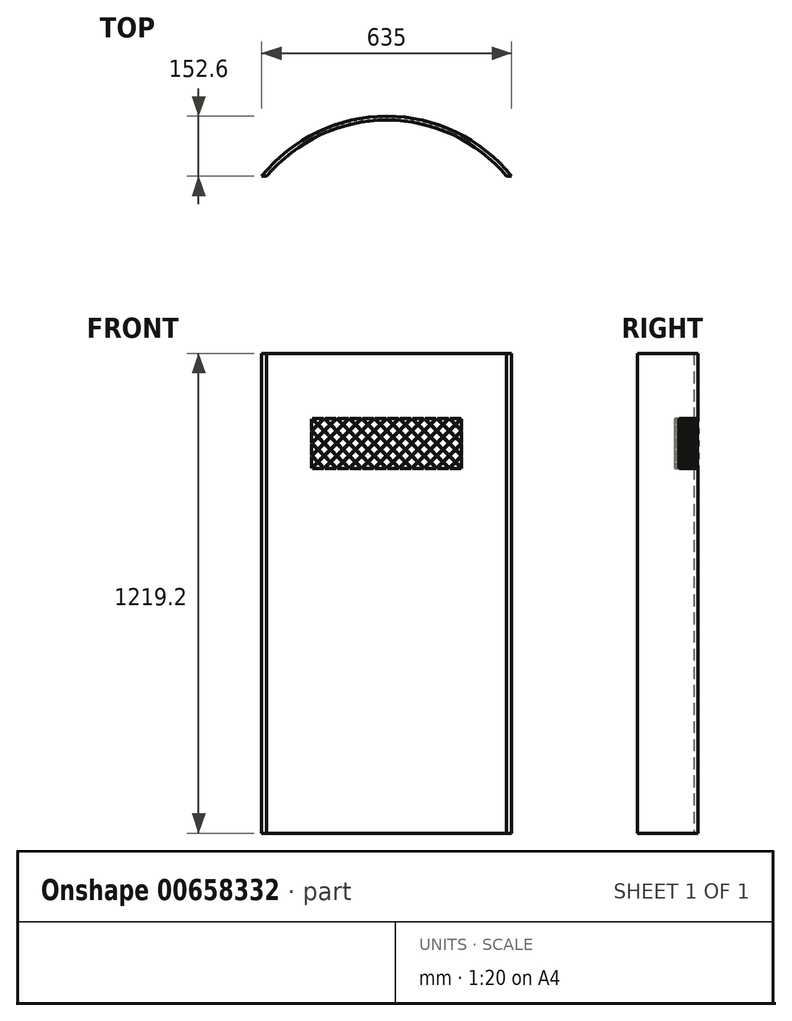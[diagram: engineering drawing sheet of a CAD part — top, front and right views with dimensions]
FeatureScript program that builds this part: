
annotation { "Feature Type Name" : "Feature", "Feature Type Description" : "" }
export const myFeature = defineFeature(function(context is Context, id is Id, definition is map)
    precondition{}
    {
        {
            var Q0;
            Q0=qCreatedBy(makeId("Top.planeOp"),FACE);
            var sketch = newSketch(context, id + "F0", { "sketchPlane" : qUnion([Q0])});
            skArc(sketch, "E0", {"start": v(304.8, 0) * mm, "mid": v(0, 142.76) * mm, "end": v(-304.8, 0) * mm});
            skArc(sketch, "E1", {"start": v(317.5, 0) * mm, "mid": v(0, 152.6) * mm, "end": v(-317.5, 0) * mm});
            skLineSegment(sketch, "E2", {"start": v(317.5, 0) * mm, "end": v(304.8, 0) * mm});
            skLineSegment(sketch, "E3", {"start": v(-304.8, 0) * mm, "end": v(-317.5, 0) * mm});
            skSolve(sketch);
        }
        {
            var Q0;
            Q0 = qSketchRegion(id + "F0", true);
            extrude(context, id + "F1", {"entities" : qUnion([Q0]), "depth" : 1219.2 * mm, "offsetDistance" : 25.4 * mm});
        }
        {
            var Q0;
            Q0=qCreatedBy(makeId("Front.planeOp"),FACE);
            var sketch = newSketch(context, id + "F2", { "sketchPlane" : qUnion([Q0])});
            skLineSegment(sketch, "E4.bottom", {"start": v(190.5, 1054.1) * mm, "end": v(-190.5, 1054.1) * mm});
            skLineSegment(sketch, "E4.top", {"start": v(190.5, 927.1) * mm, "end": v(-190.5, 927.1) * mm});
            skLineSegment(sketch, "E4.left", {"start": v(190.5, 1054.1) * mm, "end": v(190.5, 927.1) * mm});
            skLineSegment(sketch, "E4.right", {"start": v(-190.5, 1054.1) * mm, "end": v(-190.5, 927.1) * mm});
            skPoint(sketch, "E4.middle", {"position": v(0, 990.6) * mm});
            skPoint(sketch, "E5.orphan", {"position": v(-190.5, 990.6) * mm});
            skPoint(sketch, "E6.orphan", {"position": v(-63.5, 1054.1) * mm});
            skPoint(sketch, "E7.orphan", {"position": v(0, 927.1) * mm});
            skPoint(sketch, "E8.orphan", {"position": v(63.5, 1054.1) * mm});
            skPoint(sketch, "E9.end.orphan", {"position": v(190.5, 990.6) * mm});
            skPoint(sketch, "E10", {"position": v(63.5, 927.1) * mm});
            skPoint(sketch, "E11", {"position": v(-63.5, 927.1) * mm});
            skPoint(sketch, "E12", {"position": v(0, 1054.1) * mm});
            skPoint(sketch, "E13", {"position": v(127, 927.1) * mm});
            skPoint(sketch, "E14", {"position": v(127, 1054.1) * mm});
            skPoint(sketch, "E15", {"position": v(-127, 927.1) * mm});
            skPoint(sketch, "E16", {"position": v(-127, 1054.1) * mm});
            skPoint(sketch, "E17", {"position": v(190.5, 1022.35) * mm});
            skPoint(sketch, "E18", {"position": v(190.5, 958.85) * mm});
            skPoint(sketch, "E19", {"position": v(158.75, 927.1) * mm});
            skPoint(sketch, "E20", {"position": v(158.75, 1054.1) * mm});
            skPoint(sketch, "E21", {"position": v(95.25, 1054.1) * mm});
            skPoint(sketch, "E22", {"position": v(95.25, 927.1) * mm});
            skPoint(sketch, "E23", {"position": v(31.75, 927.1) * mm});
            skPoint(sketch, "E24", {"position": v(31.75, 1054.1) * mm});
            skPoint(sketch, "E25", {"position": v(-31.75, 1054.1) * mm});
            skPoint(sketch, "E26", {"position": v(-31.75, 927.1) * mm});
            skPoint(sketch, "E27", {"position": v(-95.25, 1054.1) * mm});
            skPoint(sketch, "E28", {"position": v(-95.25, 927.1) * mm});
            skPoint(sketch, "E29", {"position": v(-158.75, 927.1) * mm});
            skPoint(sketch, "E30", {"position": v(-158.75, 1054.1) * mm});
            skPoint(sketch, "E31", {"position": v(-190.5, 1022.35) * mm});
            skPoint(sketch, "E32", {"position": v(-190.5, 958.85) * mm});
            skLineSegment(sketch, "E33", {"start": v(-190.5, 1022.35) * mm, "end": v(-158.75, 1054.1) * mm});
            skLineSegment(sketch, "E34", {"start": v(-127, 1054.1) * mm, "end": v(-190.5, 990.6) * mm});
            skLineSegment(sketch, "E35", {"start": v(-190.5, 958.85) * mm, "end": v(-95.25, 1054.1) * mm});
            skLineSegment(sketch, "E36", {"start": v(-63.5, 1054.1) * mm, "end": v(-190.5, 927.1) * mm});
            skLineSegment(sketch, "E37", {"start": v(-158.75, 927.1) * mm, "end": v(-31.75, 1054.1) * mm});
            skLineSegment(sketch, "E38", {"start": v(0, 1054.1) * mm, "end": v(-127, 927.1) * mm});
            skLineSegment(sketch, "E39", {"start": v(-95.25, 927.1) * mm, "end": v(31.75, 1054.1) * mm});
            skLineSegment(sketch, "E40", {"start": v(63.5, 1054.1) * mm, "end": v(-63.5, 927.1) * mm});
            skLineSegment(sketch, "E41", {"start": v(-31.75, 927.1) * mm, "end": v(95.25, 1054.1) * mm});
            skLineSegment(sketch, "E42", {"start": v(127, 1054.1) * mm, "end": v(0, 927.1) * mm});
            skLineSegment(sketch, "E43", {"start": v(31.75, 927.1) * mm, "end": v(158.75, 1054.1) * mm});
            skLineSegment(sketch, "E44", {"start": v(190.5, 1054.1) * mm, "end": v(63.5, 927.1) * mm});
            skLineSegment(sketch, "E45", {"start": v(95.25, 927.1) * mm, "end": v(190.5, 1022.35) * mm});
            skLineSegment(sketch, "E46", {"start": v(190.5, 990.6) * mm, "end": v(127, 927.1) * mm});
            skLineSegment(sketch, "E47", {"start": v(127, 927.1) * mm, "end": v(158.75, 927.1) * mm});
            skLineSegment(sketch, "E48", {"start": v(158.75, 927.1) * mm, "end": v(158.75, 927.1) * mm});
            skLineSegment(sketch, "E49", {"start": v(190.5, 958.85) * mm, "end": v(158.75, 927.1) * mm});
            skLineSegment(sketch, "E50", {"start": v(190.5, 1022.35) * mm, "end": v(158.75, 1054.1) * mm});
            skLineSegment(sketch, "E51", {"start": v(127, 1054.1) * mm, "end": v(190.5, 990.6) * mm});
            skLineSegment(sketch, "E52", {"start": v(190.5, 958.85) * mm, "end": v(95.25, 1054.1) * mm});
            skLineSegment(sketch, "E53", {"start": v(190.5, 927.1) * mm, "end": v(63.5, 1054.1) * mm});
            skLineSegment(sketch, "E54", {"start": v(158.75, 927.1) * mm, "end": v(31.75, 1054.1) * mm});
            skLineSegment(sketch, "E55", {"start": v(0, 1054.1) * mm, "end": v(127, 927.1) * mm});
            skLineSegment(sketch, "E56", {"start": v(95.25, 927.1) * mm, "end": v(-31.75, 1054.1) * mm});
            skLineSegment(sketch, "E57", {"start": v(-63.5, 1054.1) * mm, "end": v(63.5, 927.1) * mm});
            skLineSegment(sketch, "E58", {"start": v(-95.25, 1054.1) * mm, "end": v(31.75, 927.1) * mm});
            skLineSegment(sketch, "E59", {"start": v(0, 927.1) * mm, "end": v(-127, 1054.1) * mm});
            skLineSegment(sketch, "E60", {"start": v(-158.75, 1054.1) * mm, "end": v(-31.75, 927.1) * mm});
            skLineSegment(sketch, "E61", {"start": v(-63.5, 927.1) * mm, "end": v(-190.5, 1054.1) * mm});
            skLineSegment(sketch, "E62", {"start": v(-190.5, 1022.35) * mm, "end": v(-95.25, 927.1) * mm});
            skLineSegment(sketch, "E63", {"start": v(-127, 927.1) * mm, "end": v(-190.5, 990.6) * mm});
            skLineSegment(sketch, "E64", {"start": v(-190.5, 958.85) * mm, "end": v(-158.75, 927.1) * mm});
            skLineSegment(sketch, "E65", {"start": v(-190.5, 1023.94) * mm, "end": v(-160.34, 1054.1) * mm});
            skLineSegment(sketch, "E66", {"start": v(-160.34, 1054.1) * mm, "end": v(-33.34, 927.1) * mm});
            skLineSegment(sketch, "E67", {"start": v(-33.34, 927.1) * mm, "end": v(93.66, 1054.1) * mm});
            skLineSegment(sketch, "E68", {"start": v(93.66, 1054.1) * mm, "end": v(190.5, 957.26) * mm});
            skLineSegment(sketch, "E69", {"start": v(190.5, 957.26) * mm, "end": v(160.34, 927.1) * mm});
            skLineSegment(sketch, "E70", {"start": v(160.34, 927.1) * mm, "end": v(33.34, 1054.1) * mm});
            skLineSegment(sketch, "E71", {"start": v(33.34, 1054.1) * mm, "end": v(-93.66, 927.1) * mm});
            skLineSegment(sketch, "E72", {"start": v(-93.66, 927.1) * mm, "end": v(-190.5, 1023.94) * mm});
            skLineSegment(sketch, "E73", {"start": v(-190.5, 1020.76) * mm, "end": v(-157.16, 1054.1) * mm});
            skLineSegment(sketch, "E74", {"start": v(-157.16, 1054.1) * mm, "end": v(-30.16, 927.1) * mm});
            skLineSegment(sketch, "E75", {"start": v(-30.16, 927.1) * mm, "end": v(96.84, 1054.1) * mm});
            skLineSegment(sketch, "E76", {"start": v(96.84, 1054.1) * mm, "end": v(190.5, 960.44) * mm});
            skLineSegment(sketch, "E77", {"start": v(190.5, 960.44) * mm, "end": v(157.16, 927.1) * mm});
            skLineSegment(sketch, "E78", {"start": v(157.16, 927.1) * mm, "end": v(30.16, 1054.1) * mm});
            skLineSegment(sketch, "E79", {"start": v(30.16, 1054.1) * mm, "end": v(-96.84, 927.1) * mm});
            skLineSegment(sketch, "E80", {"start": v(-96.84, 927.1) * mm, "end": v(-190.5, 1020.76) * mm});
            skLineSegment(sketch, "E81", {"start": v(-190.5, 992.19) * mm, "end": v(-128.59, 1054.1) * mm});
            skLineSegment(sketch, "E82", {"start": v(-128.59, 1054.1) * mm, "end": v(-1.59, 927.1) * mm});
            skLineSegment(sketch, "E83", {"start": v(-1.59, 927.1) * mm, "end": v(125.41, 1054.1) * mm});
            skLineSegment(sketch, "E84", {"start": v(125.41, 1054.1) * mm, "end": v(190.5, 989.01) * mm});
            skLineSegment(sketch, "E85", {"start": v(190.5, 989.01) * mm, "end": v(128.59, 927.1) * mm});
            skLineSegment(sketch, "E86", {"start": v(128.59, 927.1) * mm, "end": v(1.59, 1054.1) * mm});
            skLineSegment(sketch, "E87", {"start": v(1.59, 1054.1) * mm, "end": v(-125.41, 927.1) * mm});
            skLineSegment(sketch, "E88", {"start": v(-125.41, 927.1) * mm, "end": v(-190.5, 992.19) * mm});
            skLineSegment(sketch, "E89", {"start": v(-190.5, 989.01) * mm, "end": v(-125.41, 1054.1) * mm});
            skLineSegment(sketch, "E90", {"start": v(-125.41, 1054.1) * mm, "end": v(1.59, 927.1) * mm});
            skLineSegment(sketch, "E91", {"start": v(1.59, 927.1) * mm, "end": v(128.59, 1054.1) * mm});
            skLineSegment(sketch, "E92", {"start": v(128.59, 1054.1) * mm, "end": v(190.5, 992.19) * mm});
            skLineSegment(sketch, "E93", {"start": v(190.5, 992.19) * mm, "end": v(125.41, 927.1) * mm});
            skLineSegment(sketch, "E94", {"start": v(125.41, 927.1) * mm, "end": v(-1.59, 1054.1) * mm});
            skLineSegment(sketch, "E95", {"start": v(-1.59, 1054.1) * mm, "end": v(-128.59, 927.1) * mm});
            skLineSegment(sketch, "E96", {"start": v(-128.59, 927.1) * mm, "end": v(-190.5, 989.01) * mm});
            skLineSegment(sketch, "E97", {"start": v(-190.5, 960.44) * mm, "end": v(-96.84, 1054.1) * mm});
            skLineSegment(sketch, "E98", {"start": v(-96.84, 1054.1) * mm, "end": v(30.16, 927.1) * mm});
            skLineSegment(sketch, "E99", {"start": v(30.16, 927.1) * mm, "end": v(157.16, 1054.1) * mm});
            skLineSegment(sketch, "E100", {"start": v(157.16, 1054.1) * mm, "end": v(190.5, 1020.76) * mm});
            skLineSegment(sketch, "E101", {"start": v(190.5, 1020.76) * mm, "end": v(96.84, 927.1) * mm});
            skLineSegment(sketch, "E102", {"start": v(96.84, 927.1) * mm, "end": v(-30.16, 1054.1) * mm});
            skLineSegment(sketch, "E103", {"start": v(-30.16, 1054.1) * mm, "end": v(-157.16, 927.1) * mm});
            skLineSegment(sketch, "E104", {"start": v(-157.16, 927.1) * mm, "end": v(-190.5, 960.44) * mm});
            skLineSegment(sketch, "E105", {"start": v(-190.5, 957.26) * mm, "end": v(-93.66, 1054.1) * mm});
            skLineSegment(sketch, "E106", {"start": v(-93.66, 1054.1) * mm, "end": v(33.34, 927.1) * mm});
            skLineSegment(sketch, "E107", {"start": v(33.34, 927.1) * mm, "end": v(160.34, 1054.1) * mm});
            skLineSegment(sketch, "E108", {"start": v(160.34, 1054.1) * mm, "end": v(190.5, 1023.94) * mm});
            skLineSegment(sketch, "E109", {"start": v(190.5, 1023.94) * mm, "end": v(93.66, 927.1) * mm});
            skLineSegment(sketch, "E110", {"start": v(93.66, 927.1) * mm, "end": v(-33.34, 1054.1) * mm});
            skLineSegment(sketch, "E111", {"start": v(-33.34, 1054.1) * mm, "end": v(-160.34, 927.1) * mm});
            skLineSegment(sketch, "E112", {"start": v(-160.34, 927.1) * mm, "end": v(-190.5, 957.26) * mm});
            skLineSegment(sketch, "E113", {"start": v(-190.5, 928.69) * mm, "end": v(-65.09, 1054.1) * mm});
            skLineSegment(sketch, "E114", {"start": v(-65.09, 1054.1) * mm, "end": v(61.91, 927.1) * mm});
            skLineSegment(sketch, "E115", {"start": v(61.91, 927.1) * mm, "end": v(188.91, 1054.1) * mm});
            skLineSegment(sketch, "E116", {"start": v(190.5, 1052.51) * mm, "end": v(65.09, 927.1) * mm});
            skLineSegment(sketch, "E117", {"start": v(65.09, 927.1) * mm, "end": v(-61.91, 1054.1) * mm});
            skLineSegment(sketch, "E118", {"start": v(-61.91, 1054.1) * mm, "end": v(-188.91, 927.1) * mm});
            skLineSegment(sketch, "E119", {"start": v(-188.91, 1054.1) * mm, "end": v(-61.91, 927.1) * mm});
            skLineSegment(sketch, "E120", {"start": v(-61.91, 927.1) * mm, "end": v(65.09, 1054.1) * mm});
            skLineSegment(sketch, "E121", {"start": v(65.09, 1054.1) * mm, "end": v(190.5, 928.69) * mm});
            skLineSegment(sketch, "E122", {"start": v(188.91, 927.1) * mm, "end": v(61.91, 1054.1) * mm});
            skLineSegment(sketch, "E123", {"start": v(61.91, 1054.1) * mm, "end": v(-65.09, 927.1) * mm});
            skLineSegment(sketch, "E124", {"start": v(-65.09, 927.1) * mm, "end": v(-190.5, 1052.51) * mm});
            skSolve(sketch);
        }
        {
            var Q0;
            {var subQ0=sQuery(id+"F2.wireOp",EDGE,"E117");var subQ1=sQuery(id+"F2.wireOp",EDGE,"E75");var subQ2=makeQuery(id+"F2.imprint","INTERSECT",VERTEX,{"derivedFrom":[subQ1,subQ0]});Q0=makeQuery(id+"F2.imprint","IMPRINT",FACE,{"disambiguationData":[TD([[makeQuery(id+"F2.imprint","IMPRINT",EDGE,{"disambiguationData":[TD([[subQ2,-1.0]])],"derivedFrom":subQ1}),-1.0]])]});}
            var Q1;
            {var subQ0=sQuery(id+"F2.wireOp",EDGE,"E91");var subQ1=sQuery(id+"F2.wireOp",EDGE,"E76");var subQ2=makeQuery(id+"F2.imprint","INTERSECT",VERTEX,{"derivedFrom":[subQ1,subQ0]});Q1=makeQuery(id+"F2.imprint","IMPRINT",FACE,{"disambiguationData":[TD([[makeQuery(id+"F2.imprint","IMPRINT",EDGE,{"disambiguationData":[TD([[subQ2,-1.0]])],"derivedFrom":subQ1}),1.0]])]});}
            var Q2;
            {var subQ0=sQuery(id+"F2.wireOp",EDGE,"E86");var subQ1=sQuery(id+"F2.wireOp",EDGE,"E75");var subQ2=makeQuery(id+"F2.imprint","INTERSECT",VERTEX,{"derivedFrom":[subQ1,subQ0]});Q2=makeQuery(id+"F2.imprint","IMPRINT",FACE,{"disambiguationData":[TD([[makeQuery(id+"F2.imprint","IMPRINT",EDGE,{"disambiguationData":[TD([[subQ2,-1.0]])],"derivedFrom":subQ1}),-1.0]])]});}
            var Q3;
            {var subQ1=sQuery(id+"F2.wireOp",EDGE,"E4.top");var subQ3=sQuery(id+"F2.wireOp",EDGE,"E122");var subQ4=makeQuery(id+"F2.imprint","INTERSECT",VERTEX,{"derivedFrom":[subQ1,subQ3]});Q3=makeQuery(id+"F2.imprint","IMPRINT",FACE,{"disambiguationData":[TD([[makeQuery(id+"F2.imprint","IMPRINT",EDGE,{"disambiguationData":[TD([[subQ4,-1.0]])],"derivedFrom":subQ3}),1.0]])]});}
            var Q4;
            {var subQ0=sQuery(id+"F2.wireOp",EDGE,"E102");var subQ1=sQuery(id+"F2.wireOp",EDGE,"E67");var subQ2=makeQuery(id+"F2.imprint","INTERSECT",VERTEX,{"derivedFrom":[subQ1,subQ0]});Q4=makeQuery(id+"F2.imprint","IMPRINT",FACE,{"disambiguationData":[TD([[makeQuery(id+"F2.imprint","IMPRINT",EDGE,{"disambiguationData":[TD([[subQ2,-1.0]])],"derivedFrom":subQ1}),1.0]])]});}
            var Q5;
            {var subQ0=sQuery(id+"F2.wireOp",EDGE,"E80");var subQ3=sQuery(id+"F2.wireOp",EDGE,"E87");var subQ5=makeQuery(id+"F2.imprint","INTERSECT",VERTEX,{"derivedFrom":[subQ0,subQ3]});Q5=makeQuery(id+"F2.imprint","IMPRINT",FACE,{"disambiguationData":[TD([[makeQuery(id+"F2.imprint","IMPRINT",EDGE,{"disambiguationData":[TD([[subQ5,1.0]])],"derivedFrom":subQ0}),1.0]])]});}
            var Q6;
            {var subQ0=sQuery(id+"F2.wireOp",EDGE,"E92");var subQ3=sQuery(id+"F2.wireOp",EDGE,"E99");var subQ5=makeQuery(id+"F2.imprint","INTERSECT",VERTEX,{"derivedFrom":[subQ0,subQ3]});Q6=makeQuery(id+"F2.imprint","IMPRINT",FACE,{"disambiguationData":[TD([[makeQuery(id+"F2.imprint","IMPRINT",EDGE,{"disambiguationData":[TD([[subQ5,1.0]])],"derivedFrom":subQ0}),1.0]])]});}
            var Q7;
            {var subQ0=sQuery(id+"F2.wireOp",EDGE,"E103");var subQ1=sQuery(id+"F2.wireOp",EDGE,"E90");var subQ2=makeQuery(id+"F2.imprint","INTERSECT",VERTEX,{"derivedFrom":[subQ1,subQ0]});Q7=makeQuery(id+"F2.imprint","IMPRINT",FACE,{"disambiguationData":[TD([[makeQuery(id+"F2.imprint","IMPRINT",EDGE,{"disambiguationData":[TD([[subQ2,-1.0]])],"derivedFrom":subQ1}),1.0]])]});}
            var Q8;
            {var subQ0=sQuery(id+"F2.wireOp",EDGE,"E106");var subQ1=sQuery(id+"F2.wireOp",EDGE,"E75");var subQ2=makeQuery(id+"F2.imprint","INTERSECT",VERTEX,{"derivedFrom":[subQ1,subQ0]});Q8=makeQuery(id+"F2.imprint","IMPRINT",FACE,{"disambiguationData":[TD([[makeQuery(id+"F2.imprint","IMPRINT",EDGE,{"disambiguationData":[TD([[subQ2,-1.0]])],"derivedFrom":subQ1}),-1.0]])]});}
            var Q9;
            {var subQ0=sQuery(id+"F2.wireOp",EDGE,"E114");var subQ1=sQuery(id+"F2.wireOp",EDGE,"E79");var subQ2=makeQuery(id+"F2.imprint","INTERSECT",VERTEX,{"derivedFrom":[subQ1,subQ0]});Q9=makeQuery(id+"F2.imprint","IMPRINT",FACE,{"disambiguationData":[TD([[makeQuery(id+"F2.imprint","IMPRINT",EDGE,{"disambiguationData":[TD([[subQ2,-1.0]])],"derivedFrom":subQ1}),-1.0]])]});}
            var Q10;
            {var subQ0=sQuery(id+"F2.wireOp",EDGE,"E87");var subQ1=sQuery(id+"F2.wireOp",EDGE,"E66");var subQ2=makeQuery(id+"F2.imprint","INTERSECT",VERTEX,{"derivedFrom":[subQ1,subQ0]});Q10=makeQuery(id+"F2.imprint","IMPRINT",FACE,{"disambiguationData":[TD([[makeQuery(id+"F2.imprint","IMPRINT",EDGE,{"disambiguationData":[TD([[subQ2,-1.0]])],"derivedFrom":subQ1}),-1.0]])]});}
            var Q11;
            {var subQ0=sQuery(id+"F2.wireOp",EDGE,"E74");var subQ1=sQuery(id+"F2.wireOp",EDGE,"E67");var subQ2=makeQuery(id+"F2.imprint","INTERSECT",VERTEX,{"derivedFrom":[subQ1,subQ0]});Q11=makeQuery(id+"F2.imprint","IMPRINT",FACE,{"disambiguationData":[TD([[makeQuery(id+"F2.imprint","IMPRINT",EDGE,{"disambiguationData":[TD([[subQ2,-1.0]])],"derivedFrom":subQ1}),1.0]])]});}
            var Q12;
            {var subQ0=sQuery(id+"F2.wireOp",EDGE,"E75");var subQ3=sQuery(id+"F2.wireOp",EDGE,"E82");var subQ5=makeQuery(id+"F2.imprint","INTERSECT",VERTEX,{"derivedFrom":[subQ0,subQ3]});Q12=makeQuery(id+"F2.imprint","IMPRINT",FACE,{"disambiguationData":[TD([[makeQuery(id+"F2.imprint","IMPRINT",EDGE,{"disambiguationData":[TD([[subQ5,1.0]])],"derivedFrom":subQ0}),-1.0]])]});}
            var Q13;
            {var subQ0=sQuery(id+"F2.wireOp",EDGE,"E113");var subQ1=sQuery(id+"F2.wireOp",EDGE,"E96");var subQ2=makeQuery(id+"F2.imprint","INTERSECT",VERTEX,{"derivedFrom":[subQ1,subQ0]});Q13=makeQuery(id+"F2.imprint","IMPRINT",FACE,{"disambiguationData":[TD([[makeQuery(id+"F2.imprint","IMPRINT",EDGE,{"disambiguationData":[TD([[subQ2,-1.0]])],"derivedFrom":subQ1}),1.0]])]});}
            var Q14;
            {var subQ0=sQuery(id+"F2.wireOp",EDGE,"E90");var subQ3=sQuery(id+"F2.wireOp",EDGE,"E97");var subQ5=makeQuery(id+"F2.imprint","INTERSECT",VERTEX,{"derivedFrom":[subQ0,subQ3]});Q14=makeQuery(id+"F2.imprint","IMPRINT",FACE,{"disambiguationData":[TD([[makeQuery(id+"F2.imprint","IMPRINT",EDGE,{"disambiguationData":[TD([[subQ5,1.0]])],"derivedFrom":subQ0}),1.0]])]});}
            var Q15;
            {var subQ0=sQuery(id+"F2.wireOp",EDGE,"E102");var subQ1=sQuery(id+"F2.wireOp",EDGE,"E91");var subQ2=makeQuery(id+"F2.imprint","INTERSECT",VERTEX,{"derivedFrom":[subQ1,subQ0]});Q15=makeQuery(id+"F2.imprint","IMPRINT",FACE,{"disambiguationData":[TD([[makeQuery(id+"F2.imprint","IMPRINT",EDGE,{"disambiguationData":[TD([[subQ2,-1.0]])],"derivedFrom":subQ1}),-1.0]])]});}
            var Q16;
            {var subQ0=sQuery(id+"F2.wireOp",EDGE,"E78");var subQ3=sQuery(id+"F2.wireOp",EDGE,"E85");var subQ5=makeQuery(id+"F2.imprint","INTERSECT",VERTEX,{"derivedFrom":[subQ0,subQ3]});Q16=makeQuery(id+"F2.imprint","IMPRINT",FACE,{"disambiguationData":[TD([[makeQuery(id+"F2.imprint","IMPRINT",EDGE,{"disambiguationData":[TD([[subQ5,1.0]])],"derivedFrom":subQ0}),1.0]])]});}
            var Q17;
            {var subQ0=sQuery(id+"F2.wireOp",EDGE,"E109");var subQ1=sQuery(id+"F2.wireOp",EDGE,"E94");var subQ2=makeQuery(id+"F2.imprint","INTERSECT",VERTEX,{"derivedFrom":[subQ1,subQ0]});Q17=makeQuery(id+"F2.imprint","IMPRINT",FACE,{"disambiguationData":[TD([[makeQuery(id+"F2.imprint","IMPRINT",EDGE,{"disambiguationData":[TD([[subQ2,-1.0]])],"derivedFrom":subQ1}),1.0]])]});}
            var Q18;
            {var subQ0=sQuery(id+"F2.wireOp",EDGE,"E111");var subQ1=sQuery(id+"F2.wireOp",EDGE,"E80");var subQ2=makeQuery(id+"F2.imprint","INTERSECT",VERTEX,{"derivedFrom":[subQ1,subQ0]});Q18=makeQuery(id+"F2.imprint","IMPRINT",FACE,{"disambiguationData":[TD([[makeQuery(id+"F2.imprint","IMPRINT",EDGE,{"disambiguationData":[TD([[subQ2,-1.0]])],"derivedFrom":subQ1}),1.0]])]});}
            var Q19;
            {var subQ0=sQuery(id+"F2.wireOp",EDGE,"E96");var subQ3=sQuery(id+"F2.wireOp",EDGE,"E103");var subQ5=makeQuery(id+"F2.imprint","INTERSECT",VERTEX,{"derivedFrom":[subQ0,subQ3]});Q19=makeQuery(id+"F2.imprint","IMPRINT",FACE,{"disambiguationData":[TD([[makeQuery(id+"F2.imprint","IMPRINT",EDGE,{"disambiguationData":[TD([[subQ5,1.0]])],"derivedFrom":subQ0}),1.0]])]});}
            var Q20;
            {var subQ0=sQuery(id+"F2.wireOp",EDGE,"E111");var subQ3=sQuery(id+"F2.wireOp",EDGE,"E117");var subQ5=makeQuery(id+"F2.imprint","INTERSECT",VERTEX,{"derivedFrom":[subQ0,subQ3]});Q20=makeQuery(id+"F2.imprint","IMPRINT",FACE,{"disambiguationData":[TD([[makeQuery(id+"F2.imprint","IMPRINT",EDGE,{"disambiguationData":[TD([[subQ5,1.0]])],"derivedFrom":subQ0}),-1.0]])]});}
            var Q21;
            {var subQ0=sQuery(id+"F2.wireOp",EDGE,"E107");var subQ1=sQuery(id+"F2.wireOp",EDGE,"E92");var subQ2=makeQuery(id+"F2.imprint","INTERSECT",VERTEX,{"derivedFrom":[subQ1,subQ0]});Q21=makeQuery(id+"F2.imprint","IMPRINT",FACE,{"disambiguationData":[TD([[makeQuery(id+"F2.imprint","IMPRINT",EDGE,{"disambiguationData":[TD([[subQ2,-1.0]])],"derivedFrom":subQ1}),1.0]])]});}
            var Q22;
            {var subQ0=sQuery(id+"F2.wireOp",EDGE,"E78");var subQ1=sQuery(id+"F2.wireOp",EDGE,"E71");var subQ2=makeQuery(id+"F2.imprint","INTERSECT",VERTEX,{"derivedFrom":[subQ1,subQ0]});Q22=makeQuery(id+"F2.imprint","IMPRINT",FACE,{"disambiguationData":[TD([[makeQuery(id+"F2.imprint","IMPRINT",EDGE,{"disambiguationData":[TD([[subQ2,-1.0]])],"derivedFrom":subQ1}),1.0]])]});}
            var Q23;
            {var subQ0=sQuery(id+"F2.wireOp",EDGE,"E115");var subQ1=sQuery(id+"F2.wireOp",EDGE,"E78");var subQ2=makeQuery(id+"F2.imprint","INTERSECT",VERTEX,{"derivedFrom":[subQ1,subQ0]});Q23=makeQuery(id+"F2.imprint","IMPRINT",FACE,{"disambiguationData":[TD([[makeQuery(id+"F2.imprint","IMPRINT",EDGE,{"disambiguationData":[TD([[subQ2,-1.0]])],"derivedFrom":subQ1}),1.0]])]});}
            var Q24;
            {var subQ0=sQuery(id+"F2.wireOp",EDGE,"E109");var subQ1=sQuery(id+"F2.wireOp",EDGE,"E70");var subQ2=makeQuery(id+"F2.imprint","INTERSECT",VERTEX,{"derivedFrom":[subQ1,subQ0]});Q24=makeQuery(id+"F2.imprint","IMPRINT",FACE,{"disambiguationData":[TD([[makeQuery(id+"F2.imprint","IMPRINT",EDGE,{"disambiguationData":[TD([[subQ2,-1.0]])],"derivedFrom":subQ1}),-1.0]])]});}
            var Q25;
            {var subQ0=sQuery(id+"F2.wireOp",EDGE,"E96");var subQ3=sQuery(id+"F2.wireOp",EDGE,"E97");var subQ5=makeQuery(id+"F2.imprint","INTERSECT",VERTEX,{"derivedFrom":[subQ0,subQ3]});Q25=makeQuery(id+"F2.imprint","IMPRINT",FACE,{"disambiguationData":[TD([[makeQuery(id+"F2.imprint","IMPRINT",EDGE,{"disambiguationData":[TD([[subQ5,-1.0]])],"derivedFrom":subQ0}),1.0]])]});}
            var Q26;
            {var subQ1=sQuery(id+"F2.wireOp",EDGE,"E4.bottom");var subQ3=sQuery(id+"F2.wireOp",EDGE,"E115");var subQ4=makeQuery(id+"F2.imprint","INTERSECT",VERTEX,{"derivedFrom":[subQ1,subQ3]});Q26=makeQuery(id+"F2.imprint","IMPRINT",FACE,{"disambiguationData":[TD([[makeQuery(id+"F2.imprint","IMPRINT",EDGE,{"disambiguationData":[TD([[subQ4,1.0]])],"derivedFrom":subQ3}),1.0]])]});}
            var Q27;
            {var subQ0=sQuery(id+"F2.wireOp",EDGE,"E107");var subQ1=sQuery(id+"F2.wireOp",EDGE,"E68");var subQ2=makeQuery(id+"F2.imprint","INTERSECT",VERTEX,{"derivedFrom":[subQ1,subQ0]});Q27=makeQuery(id+"F2.imprint","IMPRINT",FACE,{"disambiguationData":[TD([[makeQuery(id+"F2.imprint","IMPRINT",EDGE,{"disambiguationData":[TD([[subQ2,-1.0]])],"derivedFrom":subQ1}),-1.0]])]});}
            var Q28;
            {var subQ0=sQuery(id+"F2.wireOp",EDGE,"E97");var subQ1=sQuery(id+"F2.wireOp",EDGE,"E80");var subQ2=makeQuery(id+"F2.imprint","INTERSECT",VERTEX,{"derivedFrom":[subQ1,subQ0]});Q28=makeQuery(id+"F2.imprint","IMPRINT",FACE,{"disambiguationData":[TD([[makeQuery(id+"F2.imprint","IMPRINT",EDGE,{"disambiguationData":[TD([[subQ2,-1.0]])],"derivedFrom":subQ1}),1.0]])]});}
            var Q29;
            {var subQ0=sQuery(id+"F2.wireOp",EDGE,"E71");var subQ3=sQuery(id+"F2.wireOp",EDGE,"E124");var subQ5=makeQuery(id+"F2.imprint","INTERSECT",VERTEX,{"derivedFrom":[subQ0,subQ3]});Q29=makeQuery(id+"F2.imprint","IMPRINT",FACE,{"disambiguationData":[TD([[makeQuery(id+"F2.imprint","IMPRINT",EDGE,{"disambiguationData":[TD([[subQ5,-1.0]])],"derivedFrom":subQ0}),1.0]])]});}
            var Q30;
            {var subQ0=sQuery(id+"F2.wireOp",EDGE,"E114");var subQ1=sQuery(id+"F2.wireOp",EDGE,"E71");var subQ2=makeQuery(id+"F2.imprint","INTERSECT",VERTEX,{"derivedFrom":[subQ1,subQ0]});Q30=makeQuery(id+"F2.imprint","IMPRINT",FACE,{"disambiguationData":[TD([[makeQuery(id+"F2.imprint","IMPRINT",EDGE,{"disambiguationData":[TD([[subQ2,-1.0]])],"derivedFrom":subQ1}),1.0]])]});}
            var Q31;
            {var subQ0=sQuery(id+"F2.wireOp",EDGE,"E102");var subQ1=sQuery(id+"F2.wireOp",EDGE,"E75");var subQ2=makeQuery(id+"F2.imprint","INTERSECT",VERTEX,{"derivedFrom":[subQ1,subQ0]});Q31=makeQuery(id+"F2.imprint","IMPRINT",FACE,{"disambiguationData":[TD([[makeQuery(id+"F2.imprint","IMPRINT",EDGE,{"disambiguationData":[TD([[subQ2,-1.0]])],"derivedFrom":subQ1}),-1.0]])]});}
            var Q32;
            {var subQ0=sQuery(id+"F2.wireOp",EDGE,"E117");var subQ1=sQuery(id+"F2.wireOp",EDGE,"E107");var subQ2=makeQuery(id+"F2.imprint","INTERSECT",VERTEX,{"derivedFrom":[subQ1,subQ0]});Q32=makeQuery(id+"F2.imprint","IMPRINT",FACE,{"disambiguationData":[TD([[makeQuery(id+"F2.imprint","IMPRINT",EDGE,{"disambiguationData":[TD([[subQ2,-1.0]])],"derivedFrom":subQ1}),-1.0]])]});}
            var Q33;
            {var subQ0=sQuery(id+"F2.wireOp",EDGE,"E77");var subQ1=sQuery(id+"F2.wireOp",EDGE,"E70");var subQ2=makeQuery(id+"F2.imprint","INTERSECT",VERTEX,{"derivedFrom":[subQ1,subQ0]});Q33=makeQuery(id+"F2.imprint","IMPRINT",FACE,{"disambiguationData":[TD([[makeQuery(id+"F2.imprint","IMPRINT",EDGE,{"disambiguationData":[TD([[subQ2,-1.0]])],"derivedFrom":subQ1}),-1.0]])]});}
            var Q34;
            {var subQ0=sQuery(id+"F2.wireOp",EDGE,"E97");var subQ1=sQuery(id+"F2.wireOp",EDGE,"E72");var subQ2=makeQuery(id+"F2.imprint","INTERSECT",VERTEX,{"derivedFrom":[subQ1,subQ0]});Q34=makeQuery(id+"F2.imprint","IMPRINT",FACE,{"disambiguationData":[TD([[makeQuery(id+"F2.imprint","IMPRINT",EDGE,{"disambiguationData":[TD([[subQ2,-1.0]])],"derivedFrom":subQ1}),-1.0]])]});}
            var Q35;
            {var subQ0=sQuery(id+"F2.wireOp",EDGE,"E118");var subQ1=sQuery(id+"F2.wireOp",EDGE,"E90");var subQ2=makeQuery(id+"F2.imprint","INTERSECT",VERTEX,{"derivedFrom":[subQ1,subQ0]});Q35=makeQuery(id+"F2.imprint","IMPRINT",FACE,{"disambiguationData":[TD([[makeQuery(id+"F2.imprint","IMPRINT",EDGE,{"disambiguationData":[TD([[subQ2,-1.0]])],"derivedFrom":subQ1}),1.0]])]});}
            var Q36;
            {var subQ0=sQuery(id+"F2.wireOp",EDGE,"E107");var subQ1=sQuery(id+"F2.wireOp",EDGE,"E76");var subQ2=makeQuery(id+"F2.imprint","INTERSECT",VERTEX,{"derivedFrom":[subQ1,subQ0]});Q36=makeQuery(id+"F2.imprint","IMPRINT",FACE,{"disambiguationData":[TD([[makeQuery(id+"F2.imprint","IMPRINT",EDGE,{"disambiguationData":[TD([[subQ2,-1.0]])],"derivedFrom":subQ1}),1.0]])]});}
            var Q37;
            {var subQ1=sQuery(id+"F2.wireOp",EDGE,"E4.right");var subQ3=sQuery(id+"F2.wireOp",EDGE,"E113");var subQ4=makeQuery(id+"F2.imprint","INTERSECT",VERTEX,{"derivedFrom":[subQ1,subQ3]});Q37=makeQuery(id+"F2.imprint","IMPRINT",FACE,{"disambiguationData":[TD([[makeQuery(id+"F2.imprint","IMPRINT",EDGE,{"disambiguationData":[TD([[subQ4,-1.0]])],"derivedFrom":subQ3}),1.0]])]});}
            var Q38;
            {var subQ0=sQuery(id+"F2.wireOp",EDGE,"E76");var subQ3=sQuery(id+"F2.wireOp",EDGE,"E85");var subQ5=makeQuery(id+"F2.imprint","INTERSECT",VERTEX,{"derivedFrom":[subQ0,subQ3]});Q38=makeQuery(id+"F2.imprint","IMPRINT",FACE,{"disambiguationData":[TD([[makeQuery(id+"F2.imprint","IMPRINT",EDGE,{"disambiguationData":[TD([[subQ5,-1.0]])],"derivedFrom":subQ0}),1.0]])]});}
            var Q39;
            {var subQ0=sQuery(id+"F2.wireOp",EDGE,"E110");var subQ1=sQuery(id+"F2.wireOp",EDGE,"E71");var subQ2=makeQuery(id+"F2.imprint","INTERSECT",VERTEX,{"derivedFrom":[subQ1,subQ0]});Q39=makeQuery(id+"F2.imprint","IMPRINT",FACE,{"disambiguationData":[TD([[makeQuery(id+"F2.imprint","IMPRINT",EDGE,{"disambiguationData":[TD([[subQ2,-1.0]])],"derivedFrom":subQ1}),1.0]])]});}
            var Q40;
            {var subQ0=sQuery(id+"F2.wireOp",EDGE,"E82");var subQ1=sQuery(id+"F2.wireOp",EDGE,"E71");var subQ2=makeQuery(id+"F2.imprint","INTERSECT",VERTEX,{"derivedFrom":[subQ1,subQ0]});Q40=makeQuery(id+"F2.imprint","IMPRINT",FACE,{"disambiguationData":[TD([[makeQuery(id+"F2.imprint","IMPRINT",EDGE,{"disambiguationData":[TD([[subQ2,-1.0]])],"derivedFrom":subQ1}),1.0]])]});}
            var Q41;
            {var subQ0=sQuery(id+"F2.wireOp",EDGE,"E111");var subQ1=sQuery(id+"F2.wireOp",EDGE,"E96");var subQ2=makeQuery(id+"F2.imprint","INTERSECT",VERTEX,{"derivedFrom":[subQ1,subQ0]});Q41=makeQuery(id+"F2.imprint","IMPRINT",FACE,{"disambiguationData":[TD([[makeQuery(id+"F2.imprint","IMPRINT",EDGE,{"disambiguationData":[TD([[subQ2,-1.0]])],"derivedFrom":subQ1}),1.0]])]});}
            var Q42;
            {var subQ0=sQuery(id+"F2.wireOp",EDGE,"E109");var subQ1=sQuery(id+"F2.wireOp",EDGE,"E78");var subQ2=makeQuery(id+"F2.imprint","INTERSECT",VERTEX,{"derivedFrom":[subQ1,subQ0]});Q42=makeQuery(id+"F2.imprint","IMPRINT",FACE,{"disambiguationData":[TD([[makeQuery(id+"F2.imprint","IMPRINT",EDGE,{"disambiguationData":[TD([[subQ2,-1.0]])],"derivedFrom":subQ1}),1.0]])]});}
            var Q43;
            {var subQ0=sQuery(id+"F2.wireOp",EDGE,"E116");var subQ1=sQuery(id+"F2.wireOp",EDGE,"E76");var subQ2=makeQuery(id+"F2.imprint","INTERSECT",VERTEX,{"derivedFrom":[subQ1,subQ0]});Q43=makeQuery(id+"F2.imprint","IMPRINT",FACE,{"disambiguationData":[TD([[makeQuery(id+"F2.imprint","IMPRINT",EDGE,{"disambiguationData":[TD([[subQ2,-1.0]])],"derivedFrom":subQ1}),1.0]])]});}
            var Q44;
            {var subQ0=sQuery(id+"F2.wireOp",EDGE,"E99");var subQ1=sQuery(id+"F2.wireOp",EDGE,"E78");var subQ2=makeQuery(id+"F2.imprint","INTERSECT",VERTEX,{"derivedFrom":[subQ1,subQ0]});Q44=makeQuery(id+"F2.imprint","IMPRINT",FACE,{"disambiguationData":[TD([[makeQuery(id+"F2.imprint","IMPRINT",EDGE,{"disambiguationData":[TD([[subQ2,-1.0]])],"derivedFrom":subQ1}),1.0]])]});}
            var Q45;
            {var subQ0=sQuery(id+"F2.wireOp",EDGE,"E116");var subQ1=sQuery(id+"F2.wireOp",EDGE,"E92");var subQ2=makeQuery(id+"F2.imprint","INTERSECT",VERTEX,{"derivedFrom":[subQ1,subQ0]});Q45=makeQuery(id+"F2.imprint","IMPRINT",FACE,{"disambiguationData":[TD([[makeQuery(id+"F2.imprint","IMPRINT",EDGE,{"disambiguationData":[TD([[subQ2,-1.0]])],"derivedFrom":subQ1}),1.0]])]});}
            var Q46;
            {var subQ0=sQuery(id+"F2.wireOp",EDGE,"E101");var subQ1=sQuery(id+"F2.wireOp",EDGE,"E76");var subQ2=makeQuery(id+"F2.imprint","INTERSECT",VERTEX,{"derivedFrom":[subQ1,subQ0]});Q46=makeQuery(id+"F2.imprint","IMPRINT",FACE,{"disambiguationData":[TD([[makeQuery(id+"F2.imprint","IMPRINT",EDGE,{"disambiguationData":[TD([[subQ2,-1.0]])],"derivedFrom":subQ1}),1.0]])]});}
            var Q47;
            {var subQ0=sQuery(id+"F2.wireOp",EDGE,"E86");var subQ1=sQuery(id+"F2.wireOp",EDGE,"E67");var subQ2=makeQuery(id+"F2.imprint","INTERSECT",VERTEX,{"derivedFrom":[subQ1,subQ0]});Q47=makeQuery(id+"F2.imprint","IMPRINT",FACE,{"disambiguationData":[TD([[makeQuery(id+"F2.imprint","IMPRINT",EDGE,{"disambiguationData":[TD([[subQ2,-1.0]])],"derivedFrom":subQ1}),1.0]])]});}
            var Q48;
            {var subQ0=sQuery(id+"F2.wireOp",EDGE,"E94");var subQ1=sQuery(id+"F2.wireOp",EDGE,"E71");var subQ2=makeQuery(id+"F2.imprint","INTERSECT",VERTEX,{"derivedFrom":[subQ1,subQ0]});Q48=makeQuery(id+"F2.imprint","IMPRINT",FACE,{"disambiguationData":[TD([[makeQuery(id+"F2.imprint","IMPRINT",EDGE,{"disambiguationData":[TD([[subQ2,-1.0]])],"derivedFrom":subQ1}),1.0]])]});}
            var Q49;
            {var subQ0=sQuery(id+"F2.wireOp",EDGE,"E114");var subQ1=sQuery(id+"F2.wireOp",EDGE,"E95");var subQ2=makeQuery(id+"F2.imprint","INTERSECT",VERTEX,{"derivedFrom":[subQ1,subQ0]});Q49=makeQuery(id+"F2.imprint","IMPRINT",FACE,{"disambiguationData":[TD([[makeQuery(id+"F2.imprint","IMPRINT",EDGE,{"disambiguationData":[TD([[subQ2,-1.0]])],"derivedFrom":subQ1}),-1.0]])]});}
            var Q50;
            {var subQ0=sQuery(id+"F2.wireOp",EDGE,"E67");var subQ3=sQuery(id+"F2.wireOp",EDGE,"E121");var subQ5=makeQuery(id+"F2.imprint","INTERSECT",VERTEX,{"derivedFrom":[subQ0,subQ3]});Q50=makeQuery(id+"F2.imprint","IMPRINT",FACE,{"disambiguationData":[TD([[makeQuery(id+"F2.imprint","IMPRINT",EDGE,{"disambiguationData":[TD([[subQ5,-1.0]])],"derivedFrom":subQ0}),1.0]])]});}
            var Q51;
            {var subQ0=sQuery(id+"F2.wireOp",EDGE,"E118");var subQ1=sQuery(id+"F2.wireOp",EDGE,"E74");var subQ2=makeQuery(id+"F2.imprint","INTERSECT",VERTEX,{"derivedFrom":[subQ1,subQ0]});Q51=makeQuery(id+"F2.imprint","IMPRINT",FACE,{"disambiguationData":[TD([[makeQuery(id+"F2.imprint","IMPRINT",EDGE,{"disambiguationData":[TD([[subQ2,-1.0]])],"derivedFrom":subQ1}),1.0]])]});}
            var Q52;
            {var subQ0=sQuery(id+"F2.wireOp",EDGE,"E93");var subQ1=sQuery(id+"F2.wireOp",EDGE,"E78");var subQ2=makeQuery(id+"F2.imprint","INTERSECT",VERTEX,{"derivedFrom":[subQ1,subQ0]});Q52=makeQuery(id+"F2.imprint","IMPRINT",FACE,{"disambiguationData":[TD([[makeQuery(id+"F2.imprint","IMPRINT",EDGE,{"disambiguationData":[TD([[subQ2,-1.0]])],"derivedFrom":subQ1}),1.0]])]});}
            var Q53;
            {var subQ0=sQuery(id+"F2.wireOp",EDGE,"E110");var subQ1=sQuery(id+"F2.wireOp",EDGE,"E95");var subQ2=makeQuery(id+"F2.imprint","INTERSECT",VERTEX,{"derivedFrom":[subQ1,subQ0]});Q53=makeQuery(id+"F2.imprint","IMPRINT",FACE,{"disambiguationData":[TD([[makeQuery(id+"F2.imprint","IMPRINT",EDGE,{"disambiguationData":[TD([[subQ2,-1.0]])],"derivedFrom":subQ1}),-1.0]])]});}
            var Q54;
            {var subQ0=sQuery(id+"F2.wireOp",EDGE,"E99");var subQ1=sQuery(id+"F2.wireOp",EDGE,"E70");var subQ2=makeQuery(id+"F2.imprint","INTERSECT",VERTEX,{"derivedFrom":[subQ1,subQ0]});Q54=makeQuery(id+"F2.imprint","IMPRINT",FACE,{"disambiguationData":[TD([[makeQuery(id+"F2.imprint","IMPRINT",EDGE,{"disambiguationData":[TD([[subQ2,-1.0]])],"derivedFrom":subQ1}),-1.0]])]});}
            var Q55;
            {var subQ0=sQuery(id+"F2.wireOp",EDGE,"E70");var subQ3=sQuery(id+"F2.wireOp",EDGE,"E123");var subQ5=makeQuery(id+"F2.imprint","INTERSECT",VERTEX,{"derivedFrom":[subQ0,subQ3]});Q55=makeQuery(id+"F2.imprint","IMPRINT",FACE,{"disambiguationData":[TD([[makeQuery(id+"F2.imprint","IMPRINT",EDGE,{"disambiguationData":[TD([[subQ5,-1.0]])],"derivedFrom":subQ0}),-1.0]])]});}
            var Q56;
            {var subQ0=sQuery(id+"F2.wireOp",EDGE,"E105");var subQ1=sQuery(id+"F2.wireOp",EDGE,"E90");var subQ2=makeQuery(id+"F2.imprint","INTERSECT",VERTEX,{"derivedFrom":[subQ1,subQ0]});Q56=makeQuery(id+"F2.imprint","IMPRINT",FACE,{"disambiguationData":[TD([[makeQuery(id+"F2.imprint","IMPRINT",EDGE,{"disambiguationData":[TD([[subQ2,-1.0]])],"derivedFrom":subQ1}),1.0]])]});}
            var Q57;
            {var subQ0=sQuery(id+"F2.wireOp",EDGE,"E113");var subQ1=sQuery(id+"F2.wireOp",EDGE,"E72");var subQ2=makeQuery(id+"F2.imprint","INTERSECT",VERTEX,{"derivedFrom":[subQ1,subQ0]});Q57=makeQuery(id+"F2.imprint","IMPRINT",FACE,{"disambiguationData":[TD([[makeQuery(id+"F2.imprint","IMPRINT",EDGE,{"disambiguationData":[TD([[subQ2,-1.0]])],"derivedFrom":subQ1}),-1.0]])]});}
            var Q58;
            {var subQ0=sQuery(id+"F2.wireOp",EDGE,"E94");var subQ1=sQuery(id+"F2.wireOp",EDGE,"E79");var subQ2=makeQuery(id+"F2.imprint","INTERSECT",VERTEX,{"derivedFrom":[subQ1,subQ0]});Q58=makeQuery(id+"F2.imprint","IMPRINT",FACE,{"disambiguationData":[TD([[makeQuery(id+"F2.imprint","IMPRINT",EDGE,{"disambiguationData":[TD([[subQ2,-1.0]])],"derivedFrom":subQ1}),-1.0]])]});}
            var Q59;
            {var subQ0=sQuery(id+"F2.wireOp",EDGE,"E103");var subQ1=sQuery(id+"F2.wireOp",EDGE,"E74");var subQ2=makeQuery(id+"F2.imprint","INTERSECT",VERTEX,{"derivedFrom":[subQ1,subQ0]});Q59=makeQuery(id+"F2.imprint","IMPRINT",FACE,{"disambiguationData":[TD([[makeQuery(id+"F2.imprint","IMPRINT",EDGE,{"disambiguationData":[TD([[subQ2,-1.0]])],"derivedFrom":subQ1}),1.0]])]});}
            var Q60;
            {var subQ0=sQuery(id+"F2.wireOp",EDGE,"E83");var subQ1=sQuery(id+"F2.wireOp",EDGE,"E70");var subQ2=makeQuery(id+"F2.imprint","INTERSECT",VERTEX,{"derivedFrom":[subQ1,subQ0]});Q60=makeQuery(id+"F2.imprint","IMPRINT",FACE,{"disambiguationData":[TD([[makeQuery(id+"F2.imprint","IMPRINT",EDGE,{"disambiguationData":[TD([[subQ2,-1.0]])],"derivedFrom":subQ1}),-1.0]])]});}
            var Q61;
            {var subQ0=sQuery(id+"F2.wireOp",EDGE,"E107");var subQ3=sQuery(id+"F2.wireOp",EDGE,"E114");var subQ5=makeQuery(id+"F2.imprint","INTERSECT",VERTEX,{"derivedFrom":[subQ0,subQ3]});Q61=makeQuery(id+"F2.imprint","IMPRINT",FACE,{"disambiguationData":[TD([[makeQuery(id+"F2.imprint","IMPRINT",EDGE,{"disambiguationData":[TD([[subQ5,1.0]])],"derivedFrom":subQ0}),-1.0]])]});}
            var Q62;
            {var subQ0=sQuery(id+"F2.wireOp",EDGE,"E103");var subQ1=sQuery(id+"F2.wireOp",EDGE,"E66");var subQ2=makeQuery(id+"F2.imprint","INTERSECT",VERTEX,{"derivedFrom":[subQ1,subQ0]});Q62=makeQuery(id+"F2.imprint","IMPRINT",FACE,{"disambiguationData":[TD([[makeQuery(id+"F2.imprint","IMPRINT",EDGE,{"disambiguationData":[TD([[subQ2,-1.0]])],"derivedFrom":subQ1}),-1.0]])]});}
            var Q63;
            {var subQ1=sQuery(id+"F2.wireOp",EDGE,"E4.bottom");var subQ3=sQuery(id+"F2.wireOp",EDGE,"E119");var subQ4=makeQuery(id+"F2.imprint","INTERSECT",VERTEX,{"derivedFrom":[subQ1,subQ3]});Q63=makeQuery(id+"F2.imprint","IMPRINT",FACE,{"disambiguationData":[TD([[makeQuery(id+"F2.imprint","IMPRINT",EDGE,{"disambiguationData":[TD([[subQ4,-1.0]])],"derivedFrom":subQ3}),1.0]])]});}
            var Q64;
            {var subQ0=sQuery(id+"F2.wireOp",EDGE,"E76");var subQ3=sQuery(id+"F2.wireOp",EDGE,"E83");var subQ5=makeQuery(id+"F2.imprint","INTERSECT",VERTEX,{"derivedFrom":[subQ0,subQ3]});Q64=makeQuery(id+"F2.imprint","IMPRINT",FACE,{"disambiguationData":[TD([[makeQuery(id+"F2.imprint","IMPRINT",EDGE,{"disambiguationData":[TD([[subQ5,1.0]])],"derivedFrom":subQ0}),1.0]])]});}
            var Q65;
            {var subQ0=sQuery(id+"F2.wireOp",EDGE,"E71");var subQ1=sQuery(id+"F2.wireOp",EDGE,"E66");var subQ2=makeQuery(id+"F2.imprint","INTERSECT",VERTEX,{"derivedFrom":[subQ1,subQ0]});Q65=makeQuery(id+"F2.imprint","IMPRINT",FACE,{"disambiguationData":[TD([[makeQuery(id+"F2.imprint","IMPRINT",EDGE,{"disambiguationData":[TD([[subQ2,-1.0]])],"derivedFrom":subQ1}),-1.0]])]});}
            var Q66;
            {var subQ0=sQuery(id+"F2.wireOp",EDGE,"E118");var subQ1=sQuery(id+"F2.wireOp",EDGE,"E66");var subQ2=makeQuery(id+"F2.imprint","INTERSECT",VERTEX,{"derivedFrom":[subQ1,subQ0]});Q66=makeQuery(id+"F2.imprint","IMPRINT",FACE,{"disambiguationData":[TD([[makeQuery(id+"F2.imprint","IMPRINT",EDGE,{"disambiguationData":[TD([[subQ2,-1.0]])],"derivedFrom":subQ1}),-1.0]])]});}
            var Q67;
            {var subQ0=sQuery(id+"F2.wireOp",EDGE,"E95");var subQ1=sQuery(id+"F2.wireOp",EDGE,"E72");var subQ2=makeQuery(id+"F2.imprint","INTERSECT",VERTEX,{"derivedFrom":[subQ1,subQ0]});Q67=makeQuery(id+"F2.imprint","IMPRINT",FACE,{"disambiguationData":[TD([[makeQuery(id+"F2.imprint","IMPRINT",EDGE,{"disambiguationData":[TD([[subQ2,-1.0]])],"derivedFrom":subQ1}),-1.0]])]});}
            var Q68;
            {var subQ0=sQuery(id+"F2.wireOp",EDGE,"E85");var subQ1=sQuery(id+"F2.wireOp",EDGE,"E68");var subQ2=makeQuery(id+"F2.imprint","INTERSECT",VERTEX,{"derivedFrom":[subQ1,subQ0]});Q68=makeQuery(id+"F2.imprint","IMPRINT",FACE,{"disambiguationData":[TD([[makeQuery(id+"F2.imprint","IMPRINT",EDGE,{"disambiguationData":[TD([[subQ2,-1.0]])],"derivedFrom":subQ1}),-1.0]])]});}
            var Q69;
            {var subQ1=sQuery(id+"F2.wireOp",EDGE,"E4.top");var subQ3=sQuery(id+"F2.wireOp",EDGE,"E118");var subQ4=makeQuery(id+"F2.imprint","INTERSECT",VERTEX,{"derivedFrom":[subQ1,subQ3]});Q69=makeQuery(id+"F2.imprint","IMPRINT",FACE,{"disambiguationData":[TD([[makeQuery(id+"F2.imprint","IMPRINT",EDGE,{"disambiguationData":[TD([[subQ4,1.0]])],"derivedFrom":subQ3}),1.0]])]});}
            var Q70;
            {var subQ0=sQuery(id+"F2.wireOp",EDGE,"E115");var subQ1=sQuery(id+"F2.wireOp",EDGE,"E70");var subQ2=makeQuery(id+"F2.imprint","INTERSECT",VERTEX,{"derivedFrom":[subQ1,subQ0]});Q70=makeQuery(id+"F2.imprint","IMPRINT",FACE,{"disambiguationData":[TD([[makeQuery(id+"F2.imprint","IMPRINT",EDGE,{"disambiguationData":[TD([[subQ2,-1.0]])],"derivedFrom":subQ1}),-1.0]])]});}
            var Q71;
            {var subQ0=sQuery(id+"F2.wireOp",EDGE,"E89");var subQ1=sQuery(id+"F2.wireOp",EDGE,"E66");var subQ2=makeQuery(id+"F2.imprint","INTERSECT",VERTEX,{"derivedFrom":[subQ1,subQ0]});Q71=makeQuery(id+"F2.imprint","IMPRINT",FACE,{"disambiguationData":[TD([[makeQuery(id+"F2.imprint","IMPRINT",EDGE,{"disambiguationData":[TD([[subQ2,-1.0]])],"derivedFrom":subQ1}),-1.0]])]});}
            var Q72;
            {var subQ0=sQuery(id+"F2.wireOp",EDGE,"E105");var subQ1=sQuery(id+"F2.wireOp",EDGE,"E74");var subQ2=makeQuery(id+"F2.imprint","INTERSECT",VERTEX,{"derivedFrom":[subQ1,subQ0]});Q72=makeQuery(id+"F2.imprint","IMPRINT",FACE,{"disambiguationData":[TD([[makeQuery(id+"F2.imprint","IMPRINT",EDGE,{"disambiguationData":[TD([[subQ2,-1.0]])],"derivedFrom":subQ1}),1.0]])]});}
            var Q73;
            {var subQ0=sQuery(id+"F2.wireOp",EDGE,"E106");var subQ1=sQuery(id+"F2.wireOp",EDGE,"E91");var subQ2=makeQuery(id+"F2.imprint","INTERSECT",VERTEX,{"derivedFrom":[subQ1,subQ0]});Q73=makeQuery(id+"F2.imprint","IMPRINT",FACE,{"disambiguationData":[TD([[makeQuery(id+"F2.imprint","IMPRINT",EDGE,{"disambiguationData":[TD([[subQ2,-1.0]])],"derivedFrom":subQ1}),-1.0]])]});}
            var Q74;
            {var subQ1=sQuery(id+"F2.wireOp",EDGE,"E4.left");var subQ3=sQuery(id+"F2.wireOp",EDGE,"E116");var subQ4=makeQuery(id+"F2.imprint","INTERSECT",VERTEX,{"derivedFrom":[subQ1,subQ3]});Q74=makeQuery(id+"F2.imprint","IMPRINT",FACE,{"disambiguationData":[TD([[makeQuery(id+"F2.imprint","IMPRINT",EDGE,{"disambiguationData":[TD([[subQ4,-1.0]])],"derivedFrom":subQ3}),1.0]])]});}
            var Q75;
            {var subQ1=sQuery(id+"F2.wireOp",EDGE,"E4.right");var subQ3=sQuery(id+"F2.wireOp",EDGE,"E124");var subQ4=makeQuery(id+"F2.imprint","INTERSECT",VERTEX,{"derivedFrom":[subQ1,subQ3]});Q75=makeQuery(id+"F2.imprint","IMPRINT",FACE,{"disambiguationData":[TD([[makeQuery(id+"F2.imprint","IMPRINT",EDGE,{"disambiguationData":[TD([[subQ4,1.0]])],"derivedFrom":subQ3}),1.0]])]});}
            var Q76;
            {var subQ0=sQuery(id+"F2.wireOp",EDGE,"E80");var subQ3=sQuery(id+"F2.wireOp",EDGE,"E81");var subQ5=makeQuery(id+"F2.imprint","INTERSECT",VERTEX,{"derivedFrom":[subQ0,subQ3]});Q76=makeQuery(id+"F2.imprint","IMPRINT",FACE,{"disambiguationData":[TD([[makeQuery(id+"F2.imprint","IMPRINT",EDGE,{"disambiguationData":[TD([[subQ5,-1.0]])],"derivedFrom":subQ0}),1.0]])]});}
            var Q77;
            {var subQ0=sQuery(id+"F2.wireOp",EDGE,"E73");var subQ1=sQuery(id+"F2.wireOp",EDGE,"E66");var subQ2=makeQuery(id+"F2.imprint","INTERSECT",VERTEX,{"derivedFrom":[subQ1,subQ0]});Q77=makeQuery(id+"F2.imprint","IMPRINT",FACE,{"disambiguationData":[TD([[makeQuery(id+"F2.imprint","IMPRINT",EDGE,{"disambiguationData":[TD([[subQ2,-1.0]])],"derivedFrom":subQ1}),-1.0]])]});}
            var Q78;
            {var subQ0=sQuery(id+"F2.wireOp",EDGE,"E79");var subQ3=sQuery(id+"F2.wireOp",EDGE,"E86");var subQ5=makeQuery(id+"F2.imprint","INTERSECT",VERTEX,{"derivedFrom":[subQ0,subQ3]});Q78=makeQuery(id+"F2.imprint","IMPRINT",FACE,{"disambiguationData":[TD([[makeQuery(id+"F2.imprint","IMPRINT",EDGE,{"disambiguationData":[TD([[subQ5,1.0]])],"derivedFrom":subQ0}),-1.0]])]});}
            var Q79;
            {var subQ0=sQuery(id+"F2.wireOp",EDGE,"E110");var subQ1=sQuery(id+"F2.wireOp",EDGE,"E79");var subQ2=makeQuery(id+"F2.imprint","INTERSECT",VERTEX,{"derivedFrom":[subQ1,subQ0]});Q79=makeQuery(id+"F2.imprint","IMPRINT",FACE,{"disambiguationData":[TD([[makeQuery(id+"F2.imprint","IMPRINT",EDGE,{"disambiguationData":[TD([[subQ2,-1.0]])],"derivedFrom":subQ1}),-1.0]])]});}
            var Q80;
            {var subQ0=sQuery(id+"F2.wireOp",EDGE,"E95");var subQ1=sQuery(id+"F2.wireOp",EDGE,"E80");var subQ2=makeQuery(id+"F2.imprint","INTERSECT",VERTEX,{"derivedFrom":[subQ1,subQ0]});Q80=makeQuery(id+"F2.imprint","IMPRINT",FACE,{"disambiguationData":[TD([[makeQuery(id+"F2.imprint","IMPRINT",EDGE,{"disambiguationData":[TD([[subQ2,-1.0]])],"derivedFrom":subQ1}),1.0]])]});}
            var Q81;
            {var subQ0=sQuery(id+"F2.wireOp",EDGE,"E101");var subQ1=sQuery(id+"F2.wireOp",EDGE,"E68");var subQ2=makeQuery(id+"F2.imprint","INTERSECT",VERTEX,{"derivedFrom":[subQ1,subQ0]});Q81=makeQuery(id+"F2.imprint","IMPRINT",FACE,{"disambiguationData":[TD([[makeQuery(id+"F2.imprint","IMPRINT",EDGE,{"disambiguationData":[TD([[subQ2,-1.0]])],"derivedFrom":subQ1}),-1.0]])]});}
            var Q82;
            {var subQ0=sQuery(id+"F2.wireOp",EDGE,"E94");var subQ3=sQuery(id+"F2.wireOp",EDGE,"E101");var subQ5=makeQuery(id+"F2.imprint","INTERSECT",VERTEX,{"derivedFrom":[subQ0,subQ3]});Q82=makeQuery(id+"F2.imprint","IMPRINT",FACE,{"disambiguationData":[TD([[makeQuery(id+"F2.imprint","IMPRINT",EDGE,{"disambiguationData":[TD([[subQ5,1.0]])],"derivedFrom":subQ0}),1.0]])]});}
            var Q83;
            {var subQ0=sQuery(id+"F2.wireOp",EDGE,"E87");var subQ1=sQuery(id+"F2.wireOp",EDGE,"E74");var subQ2=makeQuery(id+"F2.imprint","INTERSECT",VERTEX,{"derivedFrom":[subQ1,subQ0]});Q83=makeQuery(id+"F2.imprint","IMPRINT",FACE,{"disambiguationData":[TD([[makeQuery(id+"F2.imprint","IMPRINT",EDGE,{"disambiguationData":[TD([[subQ2,-1.0]])],"derivedFrom":subQ1}),1.0]])]});}
            var Q84;
            {var subQ0=sQuery(id+"F2.wireOp",EDGE,"E91");var subQ3=sQuery(id+"F2.wireOp",EDGE,"E98");var subQ5=makeQuery(id+"F2.imprint","INTERSECT",VERTEX,{"derivedFrom":[subQ0,subQ3]});Q84=makeQuery(id+"F2.imprint","IMPRINT",FACE,{"disambiguationData":[TD([[makeQuery(id+"F2.imprint","IMPRINT",EDGE,{"disambiguationData":[TD([[subQ5,1.0]])],"derivedFrom":subQ0}),-1.0]])]});}
            var Q85;
            {var subQ0=sQuery(id+"F2.wireOp",EDGE,"E117");var subQ1=sQuery(id+"F2.wireOp",EDGE,"E67");var subQ2=makeQuery(id+"F2.imprint","INTERSECT",VERTEX,{"derivedFrom":[subQ1,subQ0]});Q85=makeQuery(id+"F2.imprint","IMPRINT",FACE,{"disambiguationData":[TD([[makeQuery(id+"F2.imprint","IMPRINT",EDGE,{"disambiguationData":[TD([[subQ2,-1.0]])],"derivedFrom":subQ1}),1.0]])]});}
            var Q86;
            {var subQ0=sQuery(id+"F2.wireOp",EDGE,"E81");var subQ1=sQuery(id+"F2.wireOp",EDGE,"E72");var subQ2=makeQuery(id+"F2.imprint","INTERSECT",VERTEX,{"derivedFrom":[subQ1,subQ0]});Q86=makeQuery(id+"F2.imprint","IMPRINT",FACE,{"disambiguationData":[TD([[makeQuery(id+"F2.imprint","IMPRINT",EDGE,{"disambiguationData":[TD([[subQ2,-1.0]])],"derivedFrom":subQ1}),-1.0]])]});}
            var Q87;
            {var subQ1=sQuery(id+"F2.wireOp",EDGE,"E4.left");var subQ3=sQuery(id+"F2.wireOp",EDGE,"E121");var subQ4=makeQuery(id+"F2.imprint","INTERSECT",VERTEX,{"derivedFrom":[subQ1,subQ3]});Q87=makeQuery(id+"F2.imprint","IMPRINT",FACE,{"disambiguationData":[TD([[makeQuery(id+"F2.imprint","IMPRINT",EDGE,{"disambiguationData":[TD([[subQ4,1.0]])],"derivedFrom":subQ3}),1.0]])]});}
            var Q88;
            {var subQ0=sQuery(id+"F2.wireOp",EDGE,"E74");var subQ3=sQuery(id+"F2.wireOp",EDGE,"E81");var subQ5=makeQuery(id+"F2.imprint","INTERSECT",VERTEX,{"derivedFrom":[subQ0,subQ3]});Q88=makeQuery(id+"F2.imprint","IMPRINT",FACE,{"disambiguationData":[TD([[makeQuery(id+"F2.imprint","IMPRINT",EDGE,{"disambiguationData":[TD([[subQ5,1.0]])],"derivedFrom":subQ0}),1.0]])]});}
            var Q89;
            {var subQ0=sQuery(id+"F2.wireOp",EDGE,"E95");var subQ3=sQuery(id+"F2.wireOp",EDGE,"E102");var subQ5=makeQuery(id+"F2.imprint","INTERSECT",VERTEX,{"derivedFrom":[subQ0,subQ3]});Q89=makeQuery(id+"F2.imprint","IMPRINT",FACE,{"disambiguationData":[TD([[makeQuery(id+"F2.imprint","IMPRINT",EDGE,{"disambiguationData":[TD([[subQ5,1.0]])],"derivedFrom":subQ0}),-1.0]])]});}
            var Q90;
            {var subQ0=sQuery(id+"F2.wireOp",EDGE,"E91");var subQ1=sQuery(id+"F2.wireOp",EDGE,"E68");var subQ2=makeQuery(id+"F2.imprint","INTERSECT",VERTEX,{"derivedFrom":[subQ1,subQ0]});Q90=makeQuery(id+"F2.imprint","IMPRINT",FACE,{"disambiguationData":[TD([[makeQuery(id+"F2.imprint","IMPRINT",EDGE,{"disambiguationData":[TD([[subQ2,-1.0]])],"derivedFrom":subQ1}),-1.0]])]});}
            var Q91;
            {var subQ0=sQuery(id+"F2.wireOp",EDGE,"E70");var subQ1=sQuery(id+"F2.wireOp",EDGE,"E67");var subQ2=makeQuery(id+"F2.imprint","INTERSECT",VERTEX,{"derivedFrom":[subQ1,subQ0]});Q91=makeQuery(id+"F2.imprint","IMPRINT",FACE,{"disambiguationData":[TD([[makeQuery(id+"F2.imprint","IMPRINT",EDGE,{"disambiguationData":[TD([[subQ2,-1.0]])],"derivedFrom":subQ1}),1.0]])]});}
            var Q92;
            {var subQ0=sQuery(id+"F2.wireOp",EDGE,"E118");var subQ1=sQuery(id+"F2.wireOp",EDGE,"E106");var subQ2=makeQuery(id+"F2.imprint","INTERSECT",VERTEX,{"derivedFrom":[subQ1,subQ0]});Q92=makeQuery(id+"F2.imprint","IMPRINT",FACE,{"disambiguationData":[TD([[makeQuery(id+"F2.imprint","IMPRINT",EDGE,{"disambiguationData":[TD([[subQ2,-1.0]])],"derivedFrom":subQ1}),1.0]])]});}
            var Q93;
            {var subQ0=sQuery(id+"F2.wireOp",EDGE,"E105");var subQ1=sQuery(id+"F2.wireOp",EDGE,"E66");var subQ2=makeQuery(id+"F2.imprint","INTERSECT",VERTEX,{"derivedFrom":[subQ1,subQ0]});Q93=makeQuery(id+"F2.imprint","IMPRINT",FACE,{"disambiguationData":[TD([[makeQuery(id+"F2.imprint","IMPRINT",EDGE,{"disambiguationData":[TD([[subQ2,-1.0]])],"derivedFrom":subQ1}),-1.0]])]});}
            var Q94;
            {var subQ0=sQuery(id+"F2.wireOp",EDGE,"E115");var subQ1=sQuery(id+"F2.wireOp",EDGE,"E94");var subQ2=makeQuery(id+"F2.imprint","INTERSECT",VERTEX,{"derivedFrom":[subQ1,subQ0]});Q94=makeQuery(id+"F2.imprint","IMPRINT",FACE,{"disambiguationData":[TD([[makeQuery(id+"F2.imprint","IMPRINT",EDGE,{"disambiguationData":[TD([[subQ2,-1.0]])],"derivedFrom":subQ1}),1.0]])]});}
            var Q95;
            {var subQ0=sQuery(id+"F2.wireOp",EDGE,"E106");var subQ1=sQuery(id+"F2.wireOp",EDGE,"E67");var subQ2=makeQuery(id+"F2.imprint","INTERSECT",VERTEX,{"derivedFrom":[subQ1,subQ0]});Q95=makeQuery(id+"F2.imprint","IMPRINT",FACE,{"disambiguationData":[TD([[makeQuery(id+"F2.imprint","IMPRINT",EDGE,{"disambiguationData":[TD([[subQ2,-1.0]])],"derivedFrom":subQ1}),1.0]])]});}
            var Q96;
            {var subQ0=sQuery(id+"F2.wireOp",EDGE,"E90");var subQ1=sQuery(id+"F2.wireOp",EDGE,"E67");var subQ2=makeQuery(id+"F2.imprint","INTERSECT",VERTEX,{"derivedFrom":[subQ1,subQ0]});Q96=makeQuery(id+"F2.imprint","IMPRINT",FACE,{"disambiguationData":[TD([[makeQuery(id+"F2.imprint","IMPRINT",EDGE,{"disambiguationData":[TD([[subQ2,-1.0]])],"derivedFrom":subQ1}),1.0]])]});}
            var Q97;
            {var subQ0=sQuery(id+"F2.wireOp",EDGE,"E66");var subQ3=sQuery(id+"F2.wireOp",EDGE,"E120");var subQ5=makeQuery(id+"F2.imprint","INTERSECT",VERTEX,{"derivedFrom":[subQ0,subQ3]});Q97=makeQuery(id+"F2.imprint","IMPRINT",FACE,{"disambiguationData":[TD([[makeQuery(id+"F2.imprint","IMPRINT",EDGE,{"disambiguationData":[TD([[subQ5,-1.0]])],"derivedFrom":subQ0}),-1.0]])]});}
            var Q98;
            {var subQ0=sQuery(id+"F2.wireOp",EDGE,"E98");var subQ1=sQuery(id+"F2.wireOp",EDGE,"E79");var subQ2=makeQuery(id+"F2.imprint","INTERSECT",VERTEX,{"derivedFrom":[subQ1,subQ0]});Q98=makeQuery(id+"F2.imprint","IMPRINT",FACE,{"disambiguationData":[TD([[makeQuery(id+"F2.imprint","IMPRINT",EDGE,{"disambiguationData":[TD([[subQ2,-1.0]])],"derivedFrom":subQ1}),-1.0]])]});}
            var Q99;
            {var subQ0=sQuery(id+"F2.wireOp",EDGE,"E110");var subQ3=sQuery(id+"F2.wireOp",EDGE,"E116");var subQ5=makeQuery(id+"F2.imprint","INTERSECT",VERTEX,{"derivedFrom":[subQ0,subQ3]});Q99=makeQuery(id+"F2.imprint","IMPRINT",FACE,{"disambiguationData":[TD([[makeQuery(id+"F2.imprint","IMPRINT",EDGE,{"disambiguationData":[TD([[subQ5,1.0]])],"derivedFrom":subQ0}),1.0]])]});}
            var Q100;
            {var subQ0=sQuery(id+"F2.wireOp",EDGE,"E79");var subQ1=sQuery(id+"F2.wireOp",EDGE,"E72");var subQ2=makeQuery(id+"F2.imprint","INTERSECT",VERTEX,{"derivedFrom":[subQ1,subQ0]});Q100=makeQuery(id+"F2.imprint","IMPRINT",FACE,{"disambiguationData":[TD([[makeQuery(id+"F2.imprint","IMPRINT",EDGE,{"disambiguationData":[TD([[subQ2,-1.0]])],"derivedFrom":subQ1}),-1.0]])]});}
            var Q101;
            {var subQ0=sQuery(id+"F2.wireOp",EDGE,"E75");var subQ1=sQuery(id+"F2.wireOp",EDGE,"E68");var subQ2=makeQuery(id+"F2.imprint","INTERSECT",VERTEX,{"derivedFrom":[subQ1,subQ0]});Q101=makeQuery(id+"F2.imprint","IMPRINT",FACE,{"disambiguationData":[TD([[makeQuery(id+"F2.imprint","IMPRINT",EDGE,{"disambiguationData":[TD([[subQ2,-1.0]])],"derivedFrom":subQ1}),-1.0]])]});}
            var Q102;
            {var subQ0=sQuery(id+"F2.wireOp",EDGE,"E89");var subQ1=sQuery(id+"F2.wireOp",EDGE,"E74");var subQ2=makeQuery(id+"F2.imprint","INTERSECT",VERTEX,{"derivedFrom":[subQ1,subQ0]});Q102=makeQuery(id+"F2.imprint","IMPRINT",FACE,{"disambiguationData":[TD([[makeQuery(id+"F2.imprint","IMPRINT",EDGE,{"disambiguationData":[TD([[subQ2,-1.0]])],"derivedFrom":subQ1}),1.0]])]});}
            var Q103;
            {var subQ0=sQuery(id+"F2.wireOp",EDGE,"E106");var subQ3=sQuery(id+"F2.wireOp",EDGE,"E113");var subQ5=makeQuery(id+"F2.imprint","INTERSECT",VERTEX,{"derivedFrom":[subQ0,subQ3]});Q103=makeQuery(id+"F2.imprint","IMPRINT",FACE,{"disambiguationData":[TD([[makeQuery(id+"F2.imprint","IMPRINT",EDGE,{"disambiguationData":[TD([[subQ5,1.0]])],"derivedFrom":subQ0}),1.0]])]});}
            var Q104;
            {var subQ0=sQuery(id+"F2.wireOp",EDGE,"E116");var subQ1=sQuery(id+"F2.wireOp",EDGE,"E68");var subQ2=makeQuery(id+"F2.imprint","INTERSECT",VERTEX,{"derivedFrom":[subQ1,subQ0]});Q104=makeQuery(id+"F2.imprint","IMPRINT",FACE,{"disambiguationData":[TD([[makeQuery(id+"F2.imprint","IMPRINT",EDGE,{"disambiguationData":[TD([[subQ2,-1.0]])],"derivedFrom":subQ1}),-1.0]])]});}
            var Q105;
            {var subQ0=sQuery(id+"F2.wireOp",EDGE,"E93");var subQ1=sQuery(id+"F2.wireOp",EDGE,"E70");var subQ2=makeQuery(id+"F2.imprint","INTERSECT",VERTEX,{"derivedFrom":[subQ1,subQ0]});Q105=makeQuery(id+"F2.imprint","IMPRINT",FACE,{"disambiguationData":[TD([[makeQuery(id+"F2.imprint","IMPRINT",EDGE,{"disambiguationData":[TD([[subQ2,-1.0]])],"derivedFrom":subQ1}),-1.0]])]});}
            var Q106;
            {var subQ0=sQuery(id+"F2.wireOp",EDGE,"E98");var subQ1=sQuery(id+"F2.wireOp",EDGE,"E71");var subQ2=makeQuery(id+"F2.imprint","INTERSECT",VERTEX,{"derivedFrom":[subQ1,subQ0]});Q106=makeQuery(id+"F2.imprint","IMPRINT",FACE,{"disambiguationData":[TD([[makeQuery(id+"F2.imprint","IMPRINT",EDGE,{"disambiguationData":[TD([[subQ2,-1.0]])],"derivedFrom":subQ1}),1.0]])]});}
            var Q107;
            {var subQ0=sQuery(id+"F2.wireOp",EDGE,"E92");var subQ3=sQuery(id+"F2.wireOp",EDGE,"E101");var subQ5=makeQuery(id+"F2.imprint","INTERSECT",VERTEX,{"derivedFrom":[subQ0,subQ3]});Q107=makeQuery(id+"F2.imprint","IMPRINT",FACE,{"disambiguationData":[TD([[makeQuery(id+"F2.imprint","IMPRINT",EDGE,{"disambiguationData":[TD([[subQ5,-1.0]])],"derivedFrom":subQ0}),1.0]])]});}
            var Q108;
            {var subQ0=sQuery(id+"F2.wireOp",EDGE,"E117");var subQ1=sQuery(id+"F2.wireOp",EDGE,"E91");var subQ2=makeQuery(id+"F2.imprint","INTERSECT",VERTEX,{"derivedFrom":[subQ1,subQ0]});Q108=makeQuery(id+"F2.imprint","IMPRINT",FACE,{"disambiguationData":[TD([[makeQuery(id+"F2.imprint","IMPRINT",EDGE,{"disambiguationData":[TD([[subQ2,-1.0]])],"derivedFrom":subQ1}),-1.0]])]});}
            var Q109;
            {var subQ0=sQuery(id+"F2.wireOp",EDGE,"E90");var subQ1=sQuery(id+"F2.wireOp",EDGE,"E75");var subQ2=makeQuery(id+"F2.imprint","INTERSECT",VERTEX,{"derivedFrom":[subQ1,subQ0]});Q109=makeQuery(id+"F2.imprint","IMPRINT",FACE,{"disambiguationData":[TD([[makeQuery(id+"F2.imprint","IMPRINT",EDGE,{"disambiguationData":[TD([[subQ2,-1.0]])],"derivedFrom":subQ1}),-1.0]])]});}
            var Q110;
            {var subQ0=sQuery(id+"F2.wireOp",EDGE,"E113");var subQ1=sQuery(id+"F2.wireOp",EDGE,"E80");var subQ2=makeQuery(id+"F2.imprint","INTERSECT",VERTEX,{"derivedFrom":[subQ1,subQ0]});Q110=makeQuery(id+"F2.imprint","IMPRINT",FACE,{"disambiguationData":[TD([[makeQuery(id+"F2.imprint","IMPRINT",EDGE,{"disambiguationData":[TD([[subQ2,-1.0]])],"derivedFrom":subQ1}),1.0]])]});}
            var Q111;
            {var subQ0=sQuery(id+"F2.wireOp",EDGE,"E111");var subQ1=sQuery(id+"F2.wireOp",EDGE,"E72");var subQ2=makeQuery(id+"F2.imprint","INTERSECT",VERTEX,{"derivedFrom":[subQ1,subQ0]});Q111=makeQuery(id+"F2.imprint","IMPRINT",FACE,{"disambiguationData":[TD([[makeQuery(id+"F2.imprint","IMPRINT",EDGE,{"disambiguationData":[TD([[subQ2,-1.0]])],"derivedFrom":subQ1}),-1.0]])]});}
            extrude(context, id + "F3", {"entities" : qUnion([Q0, Q1, Q2, Q3, Q4, Q5, Q6, Q7, Q8, Q9, Q10, Q11, Q12, Q13, Q14, Q15, Q16, Q17, Q18, Q19, Q20, Q21, Q22, Q23, Q24, Q25, Q26, Q27, Q28, Q29, Q30, Q31, Q32, Q33, Q34, Q35, Q36, Q37, Q38, Q39, Q40, Q41, Q42, Q43, Q44, Q45, Q46, Q47, Q48, Q49, Q50, Q51, Q52, Q53, Q54, Q55, Q56, Q57, Q58, Q59, Q60, Q61, Q62, Q63, Q64, Q65, Q66, Q67, Q68, Q69, Q70, Q71, Q72, Q73, Q74, Q75, Q76, Q77, Q78, Q79, Q80, Q81, Q82, Q83, Q84, Q85, Q86, Q87, Q88, Q89, Q90, Q91, Q92, Q93, Q94, Q95, Q96, Q97, Q98, Q99, Q100, Q101, Q102, Q103, Q104, Q105, Q106, Q107, Q108, Q109, Q110, Q111]), "operationType" : NewBodyOperationType.REMOVE, "oppositeDirection" : true, "depth" : 254 * mm, "offsetDistance" : 25.4 * mm});
        }
    });
